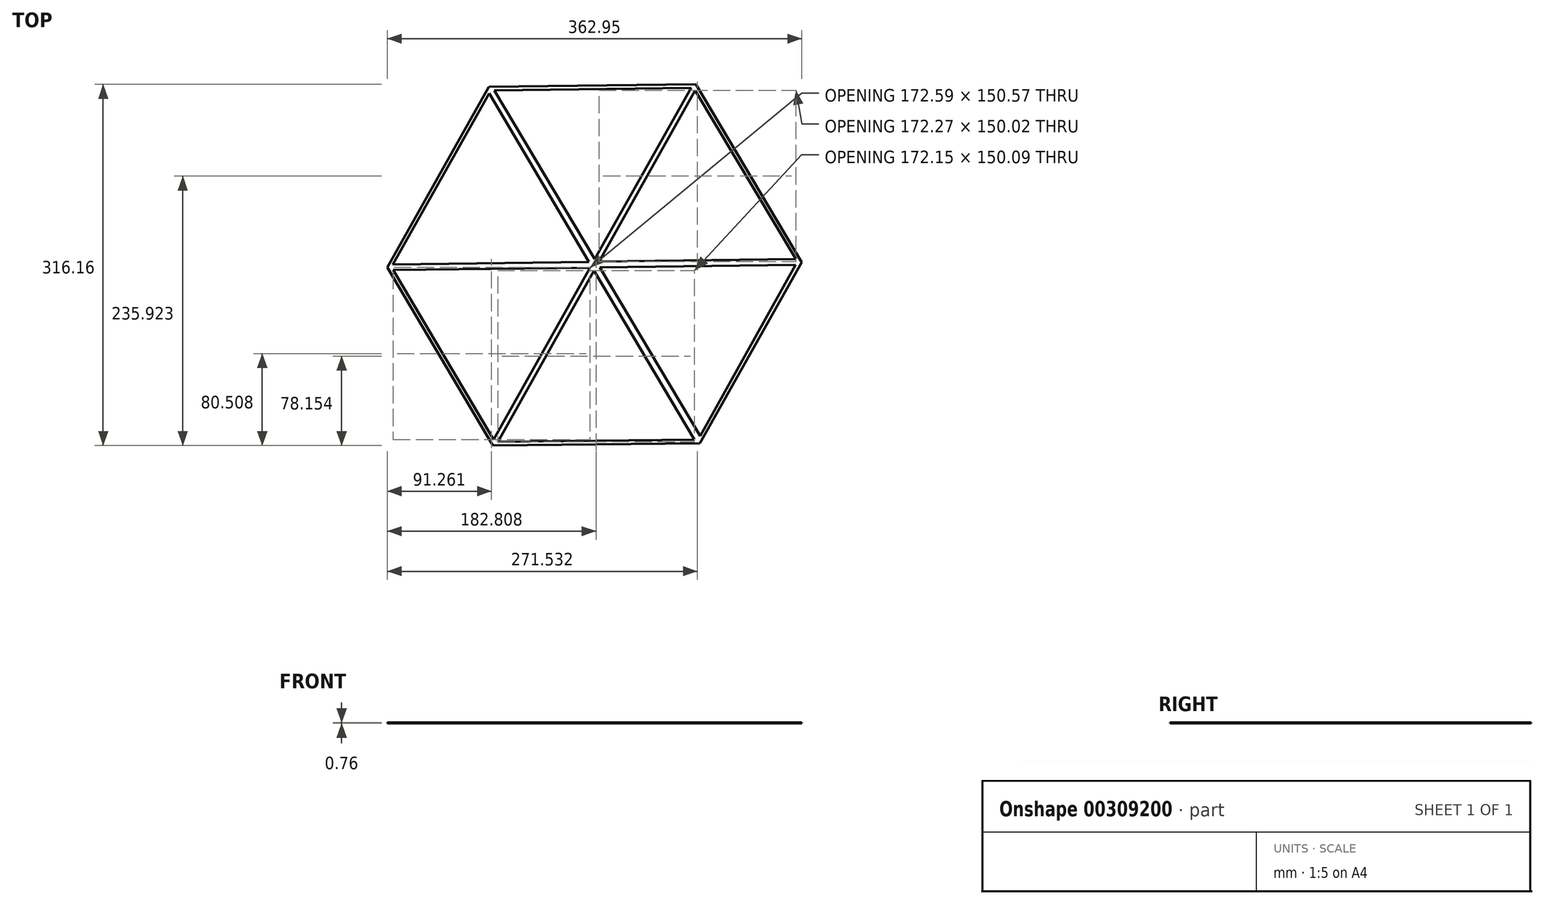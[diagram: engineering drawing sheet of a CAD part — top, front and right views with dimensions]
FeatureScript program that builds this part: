
annotation { "Feature Type Name" : "Feature", "Feature Type Description" : "" }
export const myFeature = defineFeature(function(context is Context, id is Id, definition is map)
    precondition{}
    {
        {
            var Q0;
            Q0=qCreatedBy(makeId("Top.planeOp"),FACE);
            var sketch = newSketch(context, id + "F0", { "sketchPlane" : qUnion([Q0])});
            skLineSegment(sketch, "E0.0", {"start": v(88.82, 158.08) * mm, "end": v(181.63, 2.31) * mm});
            skLineSegment(sketch, "E0.1", {"start": v(181.63, 2.31) * mm, "end": v(92.5, -155.96) * mm});
            skLineSegment(sketch, "E0.2", {"start": v(92.5, -155.96) * mm, "end": v(-88.82, -158.08) * mm});
            skLineSegment(sketch, "E0.3", {"start": v(-88.82, -158.08) * mm, "end": v(-181.32, -2.12) * mm});
            skLineSegment(sketch, "E0.4", {"start": v(-181.32, -2.12) * mm, "end": v(-92.5, 155.96) * mm});
            skLineSegment(sketch, "E0.5", {"start": v(-92.5, 155.96) * mm, "end": v(88.82, 158.08) * mm});
            skLineSegment(sketch, "E1", {"start": v(-177.78, -2.08) * mm, "end": v(-87.09, -155) * mm});
            skLineSegment(sketch, "E2", {"start": v(-87.09, -155) * mm, "end": v(90.7, -152.92) * mm});
            skLineSegment(sketch, "E3", {"start": v(90.7, -152.92) * mm, "end": v(177.78, 2.8) * mm});
            skLineSegment(sketch, "E4", {"start": v(177.78, 2.8) * mm, "end": v(87.09, 155) * mm});
            skLineSegment(sketch, "E5", {"start": v(87.09, 155) * mm, "end": v(-90.7, 152.92) * mm});
            skLineSegment(sketch, "E6", {"start": v(-90.7, 152.92) * mm, "end": v(-177.78, -2.08) * mm});
            skLineSegment(sketch, "E7", {"start": v(-88.36, -152.86) * mm, "end": v(84.6, 154.97) * mm});
            skLineSegment(sketch, "E8", {"start": v(88.37, 152.86) * mm, "end": v(-84.59, -154.97) * mm});
            skLineSegment(sketch, "E9", {"start": v(92.52, -149.65) * mm, "end": v(-87.56, 152.96) * mm});
            skLineSegment(sketch, "E10", {"start": v(-92.23, 150.2) * mm, "end": v(87.56, -152.96) * mm});
            skLineSegment(sketch, "E11", {"start": v(-176.41, 0.35) * mm, "end": v(176.35, 5.2) * mm});
            skLineSegment(sketch, "E12", {"start": v(176.22, 0) * mm, "end": v(-176.35, -4.48) * mm});
            skSolve(sketch);
        }
        {
            var Q0;
            Q0 = qSketchRegion(id + "F0", true);
            var Q1;
            {var subQ0=sQuery(id+"F0.wireOp",EDGE,"E9");var subQ1=sQuery(id+"F0.wireOp",EDGE,"E8");var subQ2=makeQuery(id+"F0.imprint","INTERSECT",VERTEX,{"derivedFrom":[subQ1,subQ0]});Q1=makeQuery(id+"F0.imprint","IMPRINT",FACE,{"disambiguationData":[TD([[makeQuery(id+"F0.imprint","IMPRINT",EDGE,{"disambiguationData":[TD([[subQ2,-1.0]])],"derivedFrom":subQ1}),1.0]])]});}
            var Q2;
            {var subQ0=sQuery(id+"F0.wireOp",EDGE,"E12");var subQ1=sQuery(id+"F0.wireOp",EDGE,"E7");var subQ2=makeQuery(id+"F0.imprint","INTERSECT",VERTEX,{"derivedFrom":[subQ1,subQ0]});Q2=makeQuery(id+"F0.imprint","IMPRINT",FACE,{"disambiguationData":[TD([[makeQuery(id+"F0.imprint","IMPRINT",EDGE,{"disambiguationData":[TD([[subQ2,-1.0]])],"derivedFrom":subQ1}),-1.0]])]});}
            var Q3;
            {var subQ0=sQuery(id+"F0.wireOp",EDGE,"E10");var subQ1=sQuery(id+"F0.wireOp",EDGE,"E7");var subQ2=makeQuery(id+"F0.imprint","INTERSECT",VERTEX,{"derivedFrom":[subQ1,subQ0]});Q3=makeQuery(id+"F0.imprint","IMPRINT",FACE,{"disambiguationData":[TD([[makeQuery(id+"F0.imprint","IMPRINT",EDGE,{"disambiguationData":[TD([[subQ2,-1.0]])],"derivedFrom":subQ1}),1.0]])]});}
            var Q4;
            {var subQ0=sQuery(id+"F0.wireOp",EDGE,"E10");var subQ1=sQuery(id+"F0.wireOp",EDGE,"E7");var subQ2=makeQuery(id+"F0.imprint","INTERSECT",VERTEX,{"derivedFrom":[subQ1,subQ0]});Q4=makeQuery(id+"F0.imprint","IMPRINT",FACE,{"disambiguationData":[TD([[makeQuery(id+"F0.imprint","IMPRINT",EDGE,{"disambiguationData":[TD([[subQ2,-1.0]])],"derivedFrom":subQ1}),-1.0]])]});}
            var Q5;
            {var subQ0=sQuery(id+"F0.wireOp",EDGE,"E11");var subQ1=sQuery(id+"F0.wireOp",EDGE,"E7");var subQ2=makeQuery(id+"F0.imprint","INTERSECT",VERTEX,{"derivedFrom":[subQ1,subQ0]});Q5=makeQuery(id+"F0.imprint","IMPRINT",FACE,{"disambiguationData":[TD([[makeQuery(id+"F0.imprint","IMPRINT",EDGE,{"disambiguationData":[TD([[subQ2,-1.0]])],"derivedFrom":subQ1}),-1.0]])]});}
            var Q6;
            {var subQ0=sQuery(id+"F0.wireOp",EDGE,"E11");var subQ1=sQuery(id+"F0.wireOp",EDGE,"E8");var subQ2=makeQuery(id+"F0.imprint","INTERSECT",VERTEX,{"derivedFrom":[subQ1,subQ0]});Q6=makeQuery(id+"F0.imprint","IMPRINT",FACE,{"disambiguationData":[TD([[makeQuery(id+"F0.imprint","IMPRINT",EDGE,{"disambiguationData":[TD([[subQ2,-1.0]])],"derivedFrom":subQ1}),-1.0]])]});}
            var Q7;
            {var subQ0=sQuery(id+"F0.wireOp",EDGE,"E12");var subQ1=sQuery(id+"F0.wireOp",EDGE,"E8");var subQ2=makeQuery(id+"F0.imprint","INTERSECT",VERTEX,{"derivedFrom":[subQ1,subQ0]});Q7=makeQuery(id+"F0.imprint","IMPRINT",FACE,{"disambiguationData":[TD([[makeQuery(id+"F0.imprint","IMPRINT",EDGE,{"disambiguationData":[TD([[subQ2,-1.0]])],"derivedFrom":subQ1}),-1.0]])]});}
            var Q8;
            {var subQ1=sQuery(id+"F0.wireOp",EDGE,"E3");var subQ5=sQuery(id+"F0.wireOp",EDGE,"E2");var subQ6=makeQuery(id+"F0.imprint","INTERSECT",VERTEX,{"derivedFrom":[subQ5,subQ1]});Q8=makeQuery(id+"F0.imprint","IMPRINT",FACE,{"disambiguationData":[TD([[makeQuery(id+"F0.imprint","IMPRINT",EDGE,{"disambiguationData":[TD([[subQ6,1.0]])],"derivedFrom":subQ5}),1.0]])]});}
            var Q9;
            {var subQ1=sQuery(id+"F0.wireOp",EDGE,"E1");var subQ5=sQuery(id+"F0.wireOp",EDGE,"E2");var subQ6=makeQuery(id+"F0.imprint","INTERSECT",VERTEX,{"derivedFrom":[subQ1,subQ5]});Q9=makeQuery(id+"F0.imprint","IMPRINT",FACE,{"disambiguationData":[TD([[makeQuery(id+"F0.imprint","IMPRINT",EDGE,{"disambiguationData":[TD([[subQ6,1.0]])],"derivedFrom":subQ1}),1.0]])]});}
            var Q10;
            {var subQ7=sQuery(id+"F0.wireOp",EDGE,"E6");var subQ8=sQuery(id+"F0.wireOp",EDGE,"E1");var subQ9=makeQuery(id+"F0.imprint","INTERSECT",VERTEX,{"derivedFrom":[subQ8,subQ7]});Q10=makeQuery(id+"F0.imprint","IMPRINT",FACE,{"disambiguationData":[TD([[makeQuery(id+"F0.imprint","IMPRINT",EDGE,{"disambiguationData":[TD([[subQ9,-1.0]])],"derivedFrom":subQ8}),1.0]])]});}
            var Q11;
            {var subQ1=sQuery(id+"F0.wireOp",EDGE,"E5");var subQ7=sQuery(id+"F0.wireOp",EDGE,"E6");var subQ8=makeQuery(id+"F0.imprint","INTERSECT",VERTEX,{"derivedFrom":[subQ1,subQ7]});Q11=makeQuery(id+"F0.imprint","IMPRINT",FACE,{"disambiguationData":[TD([[makeQuery(id+"F0.imprint","IMPRINT",EDGE,{"disambiguationData":[TD([[subQ8,1.0]])],"derivedFrom":subQ1}),1.0]])]});}
            var Q12;
            {var subQ1=sQuery(id+"F0.wireOp",EDGE,"E4");var subQ5=sQuery(id+"F0.wireOp",EDGE,"E5");var subQ6=makeQuery(id+"F0.imprint","INTERSECT",VERTEX,{"derivedFrom":[subQ1,subQ5]});Q12=makeQuery(id+"F0.imprint","IMPRINT",FACE,{"disambiguationData":[TD([[makeQuery(id+"F0.imprint","IMPRINT",EDGE,{"disambiguationData":[TD([[subQ6,1.0]])],"derivedFrom":subQ1}),1.0]])]});}
            var Q13;
            {var subQ7=sQuery(id+"F0.wireOp",EDGE,"E4");var subQ8=sQuery(id+"F0.wireOp",EDGE,"E3");var subQ9=makeQuery(id+"F0.imprint","INTERSECT",VERTEX,{"derivedFrom":[subQ8,subQ7]});Q13=makeQuery(id+"F0.imprint","IMPRINT",FACE,{"disambiguationData":[TD([[makeQuery(id+"F0.imprint","IMPRINT",EDGE,{"disambiguationData":[TD([[subQ9,1.0]])],"derivedFrom":subQ8}),1.0]])]});}
            extrude(context, id + "F1", {"entities" : qUnion([Q0, Q1, Q2, Q3, Q4, Q5, Q6, Q7, Q8, Q9, Q10, Q11, Q12, Q13]), "depth" : 0.76 * mm});
        }
    });
